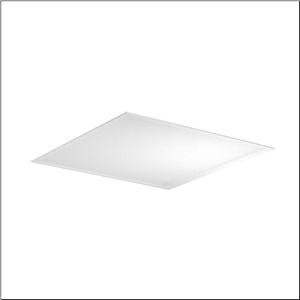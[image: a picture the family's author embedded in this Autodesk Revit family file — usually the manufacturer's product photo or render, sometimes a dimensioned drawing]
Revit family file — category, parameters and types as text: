
# Revit family: apollon_r__21_square_51mq12wd2t13_0a2d
name_source: partatom
category: Lighting Fixtures
units: mm (PartAtom-declared; Revit-internal decimal feet)

## family parameters
Cut with Voids When Loaded = No
Host = Face
Light Source = No
Part Type = Normal
Room Calculation Point = No
Round Connector Dimension = Use Diameter
Shared = No

## types (1)
- --- (1 x LED 2700 K ... 6500 K, 4000 lm, 40 W, 2700K)
    Apparent Load = 40 VA
    CIE Flux Codes = 61 87 97 100 100
    Color Rendering = 80
    Color Temperature = 2700K
    Default Elevation = 1800 mm
    Description = Apollon® 21 square, office luminaire, primary optical cover: micro prismatic cover, of PMMA, CAT 2 (L<= 3000cd/m²), light emission: direct distribution, primary light characteristic: symmetric, installation type: lay-in mounting, LED, rated luminous flux: 4.000lm, luminous efficacy: 100lm/W, light colour: 8tw, colour temperature: 2700..6500K, control gear: ECG DALI, with terminal, 5-pole, mains connection: 220..240V, AC, 50/60Hz, rated input power: 40W, housing, of aluminium, traffic white (RAL 9016), module: M600, length: 596mm, width: 596mm, height: 40mm, housing upper side, of sheet steel, galvanised, protection rating (complete): IP20, protection rating (lamp compartment, on room side): IP50, insulation class (complete): insulation class I (protective earthing), certification: CE, ENEC, permissible operating ambient temperature: -20..+40°C, packaging unit: 1 piece
    Height = 0 mm  [stored 0 ft]
    Lamp = 1 x LED 2700 K ... 6500 K
    Lamp Light Flux = 4000 lm
    Lamp Power = 40 W
    Lamp count = 1
    Length = 595 mm
    Luminous efficacy = 100 lm/W
    Manufacturer = Siteco
    ModVariant = No
    Model = 51MQ12WD2T13
    Mounting Place = Ceiling
    Mounting Type = Recessed
    Number of Poles = 1
    OnlyDefault = Yes
    Power Factor = 1
    Product Name = Apollon® 21 square
    Product group = office luminaire | ceiling recessed
    ProductGroupID = 400
    Protection Class = Protection class I
    Protection Degree = IP 20
    RLX_Detail_Level = 1
    RLX_Emergency_Light_Flux = 0 lm
    RLX_Emergency_Type = 0
    RLX_Emergency_Type_DB = No
    RlxData = <blob elided: 14701 chars, md5=9d581bdb>
    Socket = socket
    Standby Power = 0 W
    System Light Flux = 4000 lm
    System Power = 40 W
    Type Comments = individual setting: CCT=2700K
    Type Image = l_1291049.jpg
    URL = http://relux.com
    VarID = @adj_071205
    Voltage = 0 V
    Weight = 0.00 kg
    Width = 595 mm

note: [stored X ft] marks values corroborated as IEEE doubles in the binary element streams (Revit-internal decimal feet)

## geometry (parser evidence)
native form markers: Sweep x11
no freeform markers — native parametric forms only
